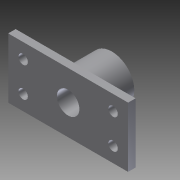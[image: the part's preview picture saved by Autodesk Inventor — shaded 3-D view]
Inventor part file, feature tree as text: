
AUTODESK INVENTOR PART (.ipt)
format: ipt  version: 2011 (Build 150239000, 239)  size: 99,840 bytes
history: native  units: in
note: dims shown in document units (in); Inventor stores cm internally (conversion verified against a paired STEP export)
features: sketch x4, extrude x3, hole x1
ambient origin geometry x8: Origin, YZ Plane, XZ Plane, XY Plane, X Axis, Y Axis, Z Axis, Center Point
bodies: Solid1 (feature_tree)
feature tree (8):
  extrude  "Extrusion1"  Depth=0.3022in TaperAngle=0.0deg
  extrude  "Extrusion2"  Depth=0.3022in TaperAngle=0.0deg
  extrude  "Extrusion3"  Depth=0.5in
  hole  "Hole1"  [1 undecoded]
  sketch  "Sketch1"  dims[d0=0.374in d1=0.3022in d2=0.0in]
  sketch  "Sketch2"  dims[d3=0.1875in d4=0.3022in d5=0.0in]
  sketch  "Sketch3"  dims[d6=1.0in d7=0.5in]
  sketch  "Sketch4"  dims[d8=0.0625in d9=0.0in d10=0.0787in d11=0.75in d12=0.375in d13=0.25in d14=0.5635in d15=1.0in d16=0.8108in]
note: 1 required parameter value undecoded (feature->parameter linkage not recoverable at this tier; creation-order binding heuristic only, values carry confidence <= 0.55)
